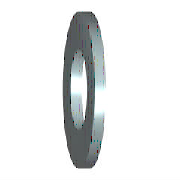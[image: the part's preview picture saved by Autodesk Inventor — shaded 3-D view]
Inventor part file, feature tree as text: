
AUTODESK INVENTOR PART (.ipt)
format: ipt  version: 2015 (Build 190159000, 159)  size: 110,080 bytes
history: native  units: mm (DEFAULTED — no unit token found)
features: other x1, plane x1, sketch x1
ambient origin geometry x7: Origin, YZ Plane, XY Plane, X Axis, Y Axis, Z Axis, Center Point
bodies: Solid1 (feature_tree), Body (feature_tree)
feature tree (3):
  other  "Work Axis1"
  plane  "Work Plane1"
  sketch  "Sketch"  dims[d0=2.2mm d1=5.0mm d2=0.3mm d3=0.0mm d4=0.0mm d5=0.0mm d6=0.0mm d7=0.0mm]
